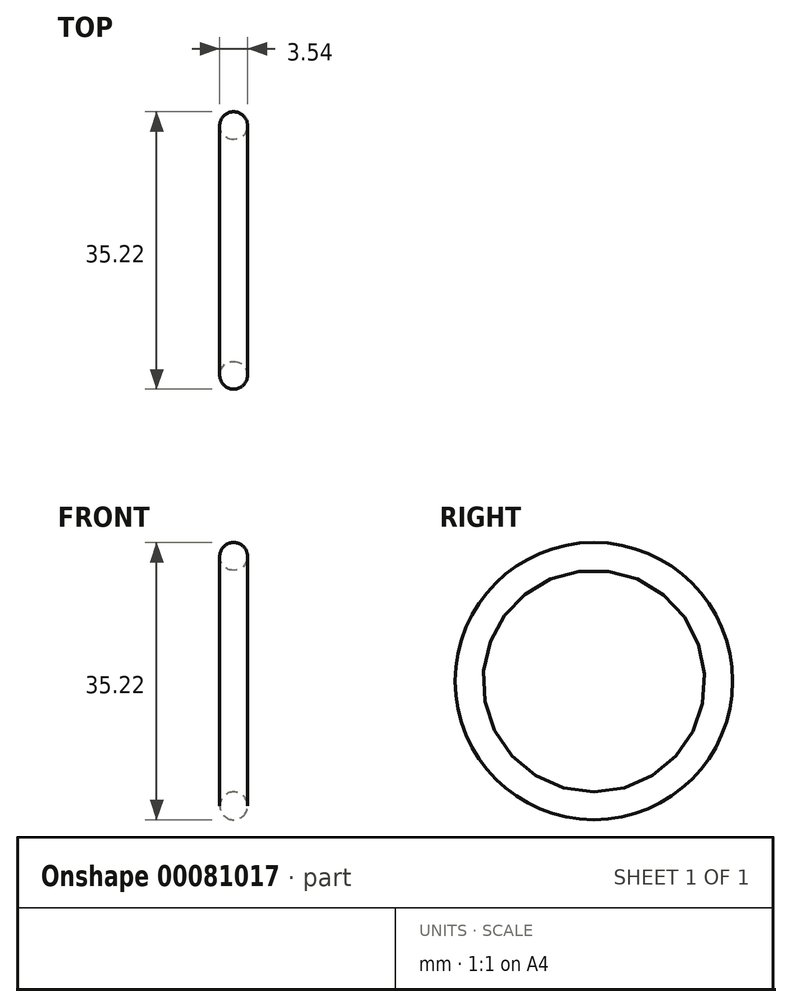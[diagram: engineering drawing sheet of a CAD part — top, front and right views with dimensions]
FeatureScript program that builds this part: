
annotation { "Feature Type Name" : "Feature", "Feature Type Description" : "" }
export const myFeature = defineFeature(function(context is Context, id is Id, definition is map)
    precondition{}
    {
        {
            var Q0;
            Q0=qCreatedBy(makeId("Front.planeOp"),FACE);
            var sketch = newSketch(context, id + "F0", { "sketchPlane" : qUnion([Q0])});
            skLineSegment(sketch, "E0", {"start": v(0, 0) * mm, "end": v(-6.06, 0) * mm, "construction": true});
            skCircle(sketch, "E1", {"center": v(0, 15.85) * mm, "radius": 1.77 * mm});
            skSolve(sketch);
        }
        {
            var Q0;
            Q0=makeQuery(id+"F0.imprint","IMPRINT",FACE,{"disambiguationData":[TD([[makeQuery(id+"F0.imprint","IMPRINT",EDGE,{"derivedFrom":sQuery(id+"F0.wireOp",EDGE,"E1")}),1.0]])]});
            var Q1;
            Q1=sQuery(id+"F0.wireOp",EDGE,"E0");
            revolve(context, id + "F1", {"entities" : qUnion([Q0]), "axis" : qUnion([Q1]), "revolveType" : RevolveType.FULL});
        }
    });
